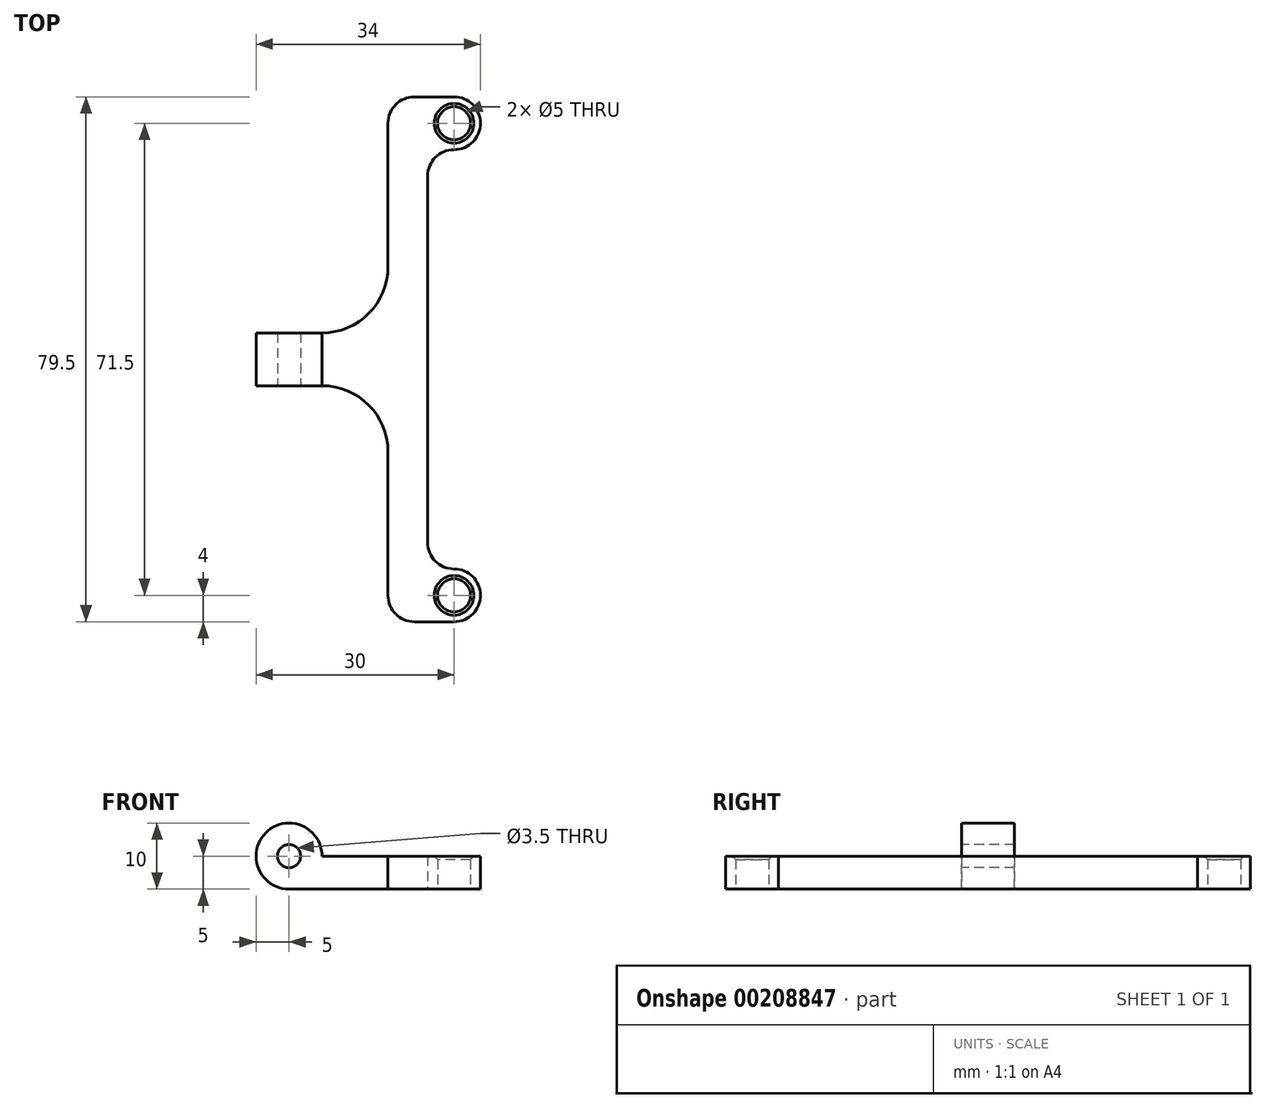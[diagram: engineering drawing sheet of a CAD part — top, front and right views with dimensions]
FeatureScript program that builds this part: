
annotation { "Feature Type Name" : "Feature", "Feature Type Description" : "" }
export const myFeature = defineFeature(function(context is Context, id is Id, definition is map)
    precondition{}
    {
        {
            var Q0;
            Q0=qCreatedBy(makeId("Top.planeOp"),FACE);
            var sketch = newSketch(context, id + "F0", { "sketchPlane" : qUnion([Q0])});
            skLineSegment(sketch, "E0", {"start": v(-26, 4) * mm, "end": v(-16, 4) * mm});
            skLineSegment(sketch, "E1", {"start": v(-6, 14) * mm, "end": v(-6, 35.75) * mm});
            skLineSegment(sketch, "E2", {"start": v(-2, 39.75) * mm, "end": v(4, 39.75) * mm});
            skLineSegment(sketch, "E3", {"start": v(4, 31.75) * mm, "end": v(4, 31.75) * mm});
            skLineSegment(sketch, "E4", {"start": v(0, 27.75) * mm, "end": v(0, 0) * mm});
            skLineSegment(sketch, "E5", {"start": v(-26, 4) * mm, "end": v(-26, 0) * mm});
            skLineSegment(sketch, "E6.MirrorCS", {"start": v(-26, -4) * mm, "end": v(-26, 0) * mm});
            skLineSegment(sketch, "E7.MirrorCS", {"start": v(-26, -4) * mm, "end": v(-16, -4) * mm});
            skLineSegment(sketch, "E8.MirrorCS", {"start": v(-6, -14) * mm, "end": v(-6, -35.75) * mm});
            skLineSegment(sketch, "E9.MirrorCS", {"start": v(-2, -39.75) * mm, "end": v(4, -39.75) * mm});
            skLineSegment(sketch, "E10.MirrorCS", {"start": v(4, -31.75) * mm, "end": v(4, -31.75) * mm});
            skLineSegment(sketch, "E11.MirrorCS", {"start": v(0, -27.75) * mm, "end": v(0, 0) * mm});
            skArc(sketch, "E12", {"start": v(4, 31.75) * mm, "mid": v(8, 35.75) * mm, "end": v(4, 39.75) * mm});
            skPoint(sketch, "E13.MirrorCS.end.orphan", {"position": v(4, -31.75) * mm});
            skPoint(sketch, "E13.MirrorCS.start.orphan", {"position": v(4, -39.75) * mm});
            skArc(sketch, "E14", {"start": v(4, -39.75) * mm, "mid": v(8, -35.75) * mm, "end": v(4, -31.75) * mm});
            skCircle(sketch, "E15", {"center": v(4, 35.75) * mm, "radius": 2.5 * mm});
            skCircle(sketch, "E16", {"center": v(4, -35.75) * mm, "radius": 2.5 * mm});
            skPoint(sketch, "E17.visualSharp", {"position": v(-6, -4) * mm});
            skArc(sketch, "E17.filletArc", {"start": v(-6, -14) * mm, "mid": v(-8.93, -6.93) * mm, "end": v(-16, -4) * mm});
            skPoint(sketch, "E18.visualSharp", {"position": v(-6, 4) * mm});
            skArc(sketch, "E18.filletArc", {"start": v(-16, 4) * mm, "mid": v(-8.93, 6.93) * mm, "end": v(-6, 14) * mm});
            skPoint(sketch, "E19.visualSharp", {"position": v(-6, -39.75) * mm});
            skArc(sketch, "E19.filletArc", {"start": v(-6, -35.75) * mm, "mid": v(-4.83, -38.58) * mm, "end": v(-2, -39.75) * mm});
            skPoint(sketch, "E20.visualSharp", {"position": v(-6, 39.75) * mm});
            skArc(sketch, "E20.filletArc", {"start": v(-2, 39.75) * mm, "mid": v(-4.83, 38.58) * mm, "end": v(-6, 35.75) * mm});
            skPoint(sketch, "E21.visualSharp", {"position": v(0, 31.75) * mm});
            skArc(sketch, "E21.filletArc", {"start": v(4, 31.75) * mm, "mid": v(1.17, 30.58) * mm, "end": v(0, 27.75) * mm});
            skPoint(sketch, "E22.visualSharp", {"position": v(0, -31.75) * mm});
            skArc(sketch, "E22.filletArc", {"start": v(0, -27.75) * mm, "mid": v(1.17, -30.58) * mm, "end": v(4, -31.75) * mm});
            skSolve(sketch);
        }
        {
            var Q0;
            Q0=qSketchRegion(id+"F0",true);
            extrude(context, id + "F1", {"entities" : qUnion([Q0]), "depth" : 5 * mm});
        }
        {
            var Q0;
            Q0=qCreatedBy(makeId("Front.planeOp"),FACE);
            var sketch = newSketch(context, id + "F2", { "sketchPlane" : qUnion([Q0])});
            skCircle(sketch, "E23", {"center": v(-21, 5) * mm, "radius": 5 * mm});
            skSolve(sketch);
        }
        {
            var Q0;
            Q0=qSketchRegion(id+"F2",true);
            var Q1;
            Q1=makeQuery(id+"F1.opExtrude","SWEPT_FACE",FACE,{"disambiguationData":[OSD([sQuery(id+"F0.wireOp",EDGE,"E7.MirrorCS")])]});
            var Q2;
            Q2=makeQuery(id+"F1.opExtrude","SWEPT_FACE",FACE,{"disambiguationData":[OSD([sQuery(id+"F0.wireOp",EDGE,"E0")])]});
            extrude(context, id + "F3", {"entities" : qUnion([Q0]), "operationType" : NewBodyOperationType.ADD, "endBound" : BoundingType.UP_TO_SURFACE, "endBoundEntityFace" : qUnion([Q1]), "depth" : 25 * mm, "hasSecondDirection" : true, "secondDirectionBound" : SecondDirectionBoundingType.UP_TO_SURFACE, "secondDirectionOppositeDirection" : true, "secondDirectionBoundEntityFace" : qUnion([Q2]), "secondDirectionDepth" : 25 * mm});
        }
        {
            var Q0;
            Q0=qCreatedBy(makeId("Front.planeOp"),FACE);
            var sketch = newSketch(context, id + "F4", { "sketchPlane" : qUnion([Q0])});
            skArc(sketch, "E24", {"start": v(-26, 5) * mm, "mid": v(-24.54, 1.46) * mm, "end": v(-21, 0) * mm});
            skLineSegment(sketch, "E25", {"start": v(-26, 5) * mm, "end": v(-26, 0) * mm});
            skLineSegment(sketch, "E26", {"start": v(-26, 0) * mm, "end": v(-21, 0) * mm});
            skCircle(sketch, "E27", {"center": v(-21, 5) * mm, "radius": 1.75 * mm});
            skSolve(sketch);
        }
        {
            var Q0;
            Q0=qSketchRegion(id+"F4",true);
            extrude(context, id + "F5", {"entities" : qUnion([Q0]), "operationType" : NewBodyOperationType.REMOVE, "endBound" : BoundingType.THROUGH_ALL, "oppositeDirection" : true, "depth" : 25 * mm, "hasSecondDirection" : true, "secondDirectionBound" : SecondDirectionBoundingType.THROUGH_ALL, "secondDirectionOppositeDirection" : false, "secondDirectionDepth" : 25 * mm});
        }
        {
            var Q0;
            Q0=makeQuery(id+"F1.opExtrude","CAP_EDGE",EDGE,{"disambiguationData":[OSD([sQuery(id+"F0.wireOp",EDGE,"E15")])],"isStart":false});
            var Q1;
            Q1=makeQuery(id+"F1.opExtrude","CAP_EDGE",EDGE,{"disambiguationData":[OSD([sQuery(id+"F0.wireOp",EDGE,"E16")])],"isStart":false});
            chamfer(context, id + "F6", {"entities" : qUnion([Q0, Q1]), "width" : .5 * mm, "tangentPropagation" : true});
        }
    });
